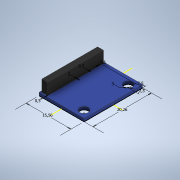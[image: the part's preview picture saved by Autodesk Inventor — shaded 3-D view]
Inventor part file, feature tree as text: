
AUTODESK INVENTOR PART (.ipt)
format: ipt  version: 2021 (Build 250183000, 183)  size: 127,488 bytes
history: native  units: mm
features: extrude x2, sketch x1
ambient origin geometry x8: Origin, YZ Plane, XZ Plane, XY Plane, X Axis, Y Axis, Z Axis, Center Point
bodies: Volumenkörper1 (feature_tree)
feature tree (3):
  sketch  "Skizze1"  dims[d0=15.56mm d1=20.26mm d2=3.0mm d3=2.5mm d4=2.5mm d5=0.5mm d6=0.5mm d7=0.5mm d8=2.0mm d9=1.0mm d10=0.0mm d11=5.0mm d12=0.0mm d13=0.5mm d14=0.872665mm]
  extrude  "Extrusion1"  Depth=20.26mm
  extrude  "Extrusion2"  Depth=0.5mm
